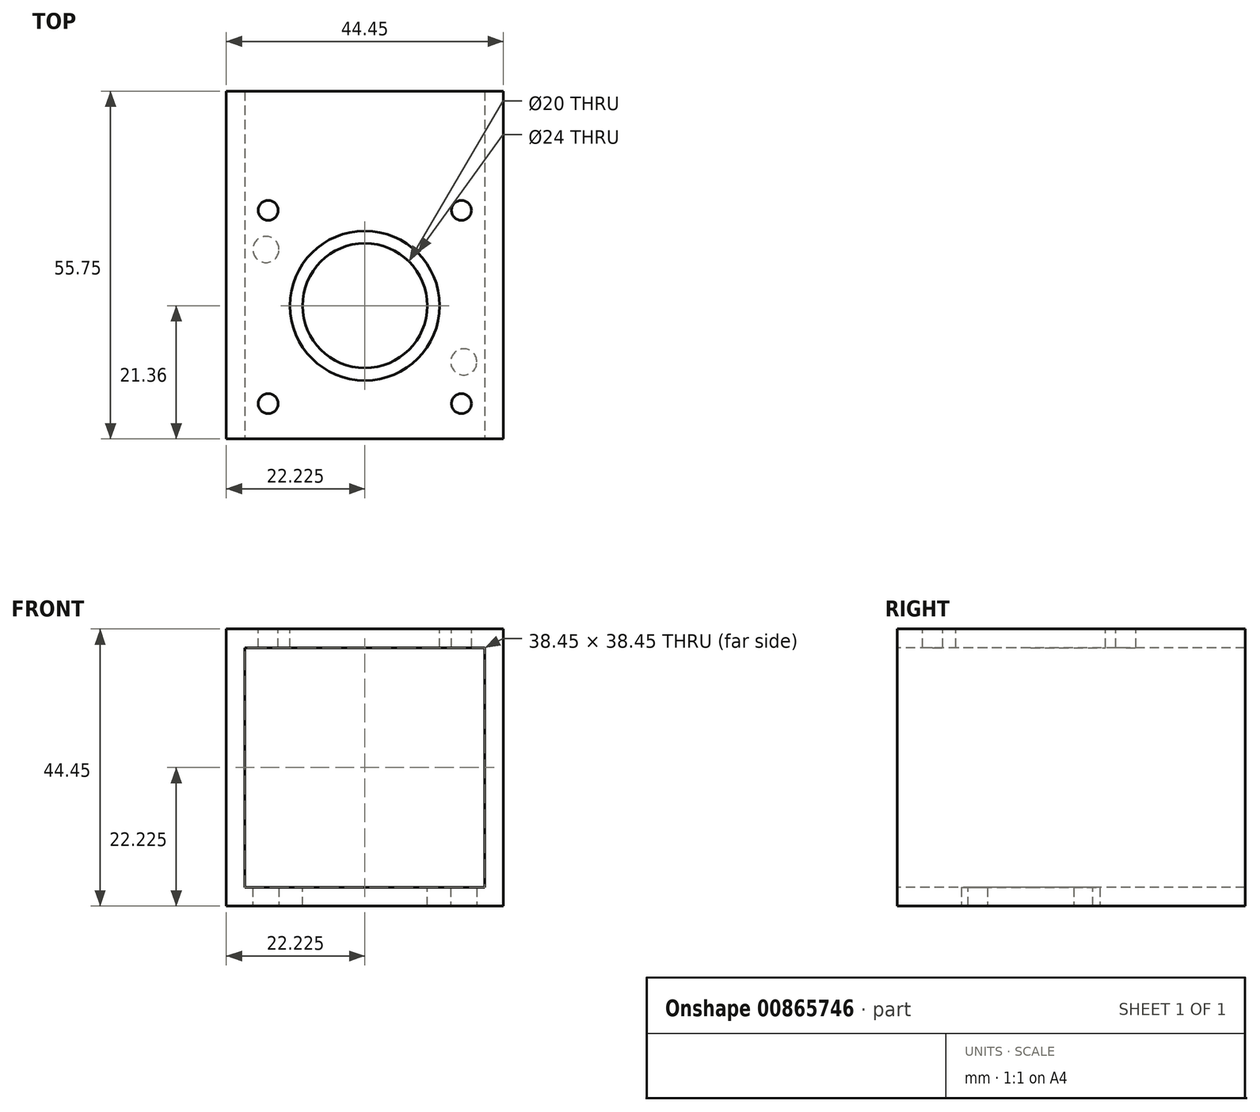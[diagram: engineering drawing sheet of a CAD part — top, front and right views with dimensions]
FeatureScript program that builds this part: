
annotation { "Feature Type Name" : "Feature", "Feature Type Description" : "" }
export const myFeature = defineFeature(function(context is Context, id is Id, definition is map)
    precondition{}
    {
        {
            var Q0;
            Q0=qCreatedBy(makeId("Front.planeOp"),FACE);
            var sketch = newSketch(context, id + "F0", { "sketchPlane" : qUnion([Q0])});
            skLineSegment(sketch, "E0.bottom", {"start": v(0, 0) * mm, "end": v(44.45, 0) * mm});
            skLineSegment(sketch, "E0.top", {"start": v(0, 44.45) * mm, "end": v(44.45, 44.45) * mm});
            skLineSegment(sketch, "E0.left", {"start": v(0, 0) * mm, "end": v(0, 44.45) * mm});
            skLineSegment(sketch, "E0.right", {"start": v(44.45, 0) * mm, "end": v(44.45, 44.45) * mm});
            skLineSegment(sketch, "E1.0", {"start": v(3, 41.45) * mm, "end": v(41.45, 41.45) * mm});
            skLineSegment(sketch, "E1.1", {"start": v(3, 3) * mm, "end": v(3, 41.45) * mm});
            skLineSegment(sketch, "E1.2", {"start": v(3, 3) * mm, "end": v(41.45, 3) * mm});
            skLineSegment(sketch, "E1.3", {"start": v(41.45, 3) * mm, "end": v(41.45, 41.45) * mm});
            skSolve(sketch);
        }
        {
            var Q0;
            Q0=qSketchRegion(id+"F0",true);
            extrude(context, id + "F1", {"entities" : qUnion([Q0]), "oppositeDirection" : true, "depth" : 55.76 * mm, "offsetDistance" : 25 * mm});
        }
        {
            var Q0;
            Q0=makeQuery(id+"F1.opExtrude","SWEPT_FACE",FACE,{"disambiguationData":[OSD([sQuery(id+"F0.wireOp",EDGE,"E0.top")])]});
            var sketch = newSketch(context, id + "F2", { "sketchPlane" : qUnion([Q0])});
            skCircle(sketch, "E2", {"center": v(22.22, 21.36) * mm, "radius": 10 * mm});
            skSolve(sketch);
        }
        {
            var Q0;
            Q0=qSketchRegion(id+"F2",true);
            extrude(context, id + "F3", {"entities" : qUnion([Q0]), "operationType" : NewBodyOperationType.REMOVE, "endBound" : BoundingType.THROUGH_ALL, "oppositeDirection" : true, "depth" : 25 * mm, "offsetDistance" : 25 * mm});
        }
        {
            var Q0;
            Q0=makeQuery(id+"F1.opExtrude","SWEPT_FACE",FACE,{"disambiguationData":[OSD([sQuery(id+"F0.wireOp",EDGE,"E0.top")])]});
            var sketch = newSketch(context, id + "F4", { "sketchPlane" : qUnion([Q0])});
            skCircle(sketch, "E3.0", {"center": v(37.73, 5.65) * mm, "radius": 1.6 * mm});
            skCircle(sketch, "E4.0", {"center": v(6.72, 5.65) * mm, "radius": 1.6 * mm});
            skCircle(sketch, "E5.0", {"center": v(37.72, 36.65) * mm, "radius": 1.6 * mm});
            skCircle(sketch, "E6.0", {"center": v(6.72, 36.65) * mm, "radius": 1.6 * mm});
            skCircle(sketch, "E7", {"center": v(22.22, 21.36) * mm, "radius": 12 * mm});
            skSolve(sketch);
        }
        {
            var Q0;
            Q0=qSketchRegion(id+"F4",true);
            extrude(context, id + "F5", {"entities" : qUnion([Q0]), "operationType" : NewBodyOperationType.REMOVE, "oppositeDirection" : true, "depth" : 5 * mm, "offsetDistance" : 25 * mm});
        }
        {
            var Q0;
            Q0=makeQuery(id+"F1.opExtrude","SWEPT_FACE",FACE,{"disambiguationData":[OSD([sQuery(id+"F0.wireOp",EDGE,"E0.bottom")])]});
            var sketch = newSketch(context, id + "F6", { "sketchPlane" : qUnion([Q0])});
            skCircle(sketch, "E8", {"center": v(38.1, -12.34) * mm, "radius": 2.1 * mm});
            skCircle(sketch, "E9", {"center": v(6.36, -30.38) * mm, "radius": 2.1 * mm});
            skSolve(sketch);
        }
        {
            var Q0;
            Q0=qSketchRegion(id+"F6",true);
            extrude(context, id + "F7", {"entities" : qUnion([Q0]), "operationType" : NewBodyOperationType.REMOVE, "oppositeDirection" : true, "depth" : 5 * mm, "offsetDistance" : 25 * mm});
        }
    });
